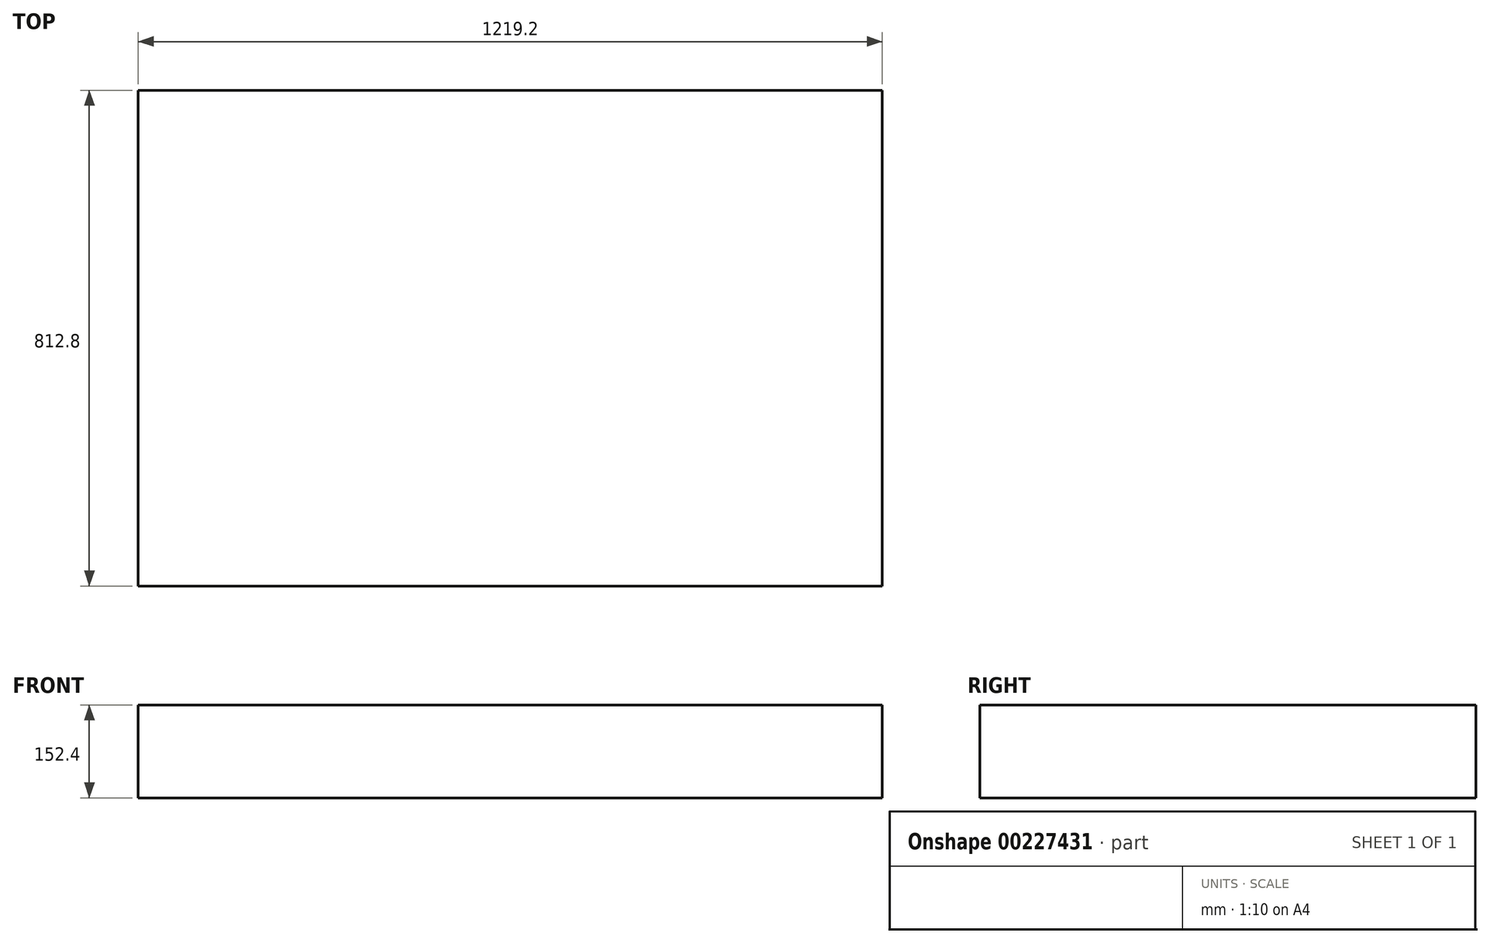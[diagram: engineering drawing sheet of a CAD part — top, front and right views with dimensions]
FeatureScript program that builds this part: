
annotation { "Feature Type Name" : "Feature", "Feature Type Description" : "" }
export const myFeature = defineFeature(function(context is Context, id is Id, definition is map)
    precondition{}
    {
        {
            var Q0;
            Q0=qCreatedBy(makeId("Top.planeOp"),FACE);
            var sketch = newSketch(context, id + "F0", { "sketchPlane" : qUnion([Q0])});
            skLineSegment(sketch, "E0.bottom", {"start": v(0, 0) * mm, "end": v(1219.2, 0) * mm});
            skLineSegment(sketch, "E0.top", {"start": v(0, 812.8) * mm, "end": v(1219.2, 812.8) * mm});
            skLineSegment(sketch, "E0.left", {"start": v(0, 0) * mm, "end": v(0, 812.8) * mm});
            skLineSegment(sketch, "E0.right", {"start": v(1219.2, 0) * mm, "end": v(1219.2, 812.8) * mm});
            skSolve(sketch);
        }
        {
            var Q0;
            Q0=makeQuery(id+"F0.imprint","IMPRINT",FACE,{"disambiguationData":[TD([[makeQuery(id+"F0.imprint","IMPRINT",EDGE,{"derivedFrom":sQuery(id+"F0.wireOp",EDGE,"E0.bottom")}),1.0]])]});
            extrude(context, id + "F1", {"entities" : qUnion([Q0]), "depth" : 152.4 * mm});
        }
    });
